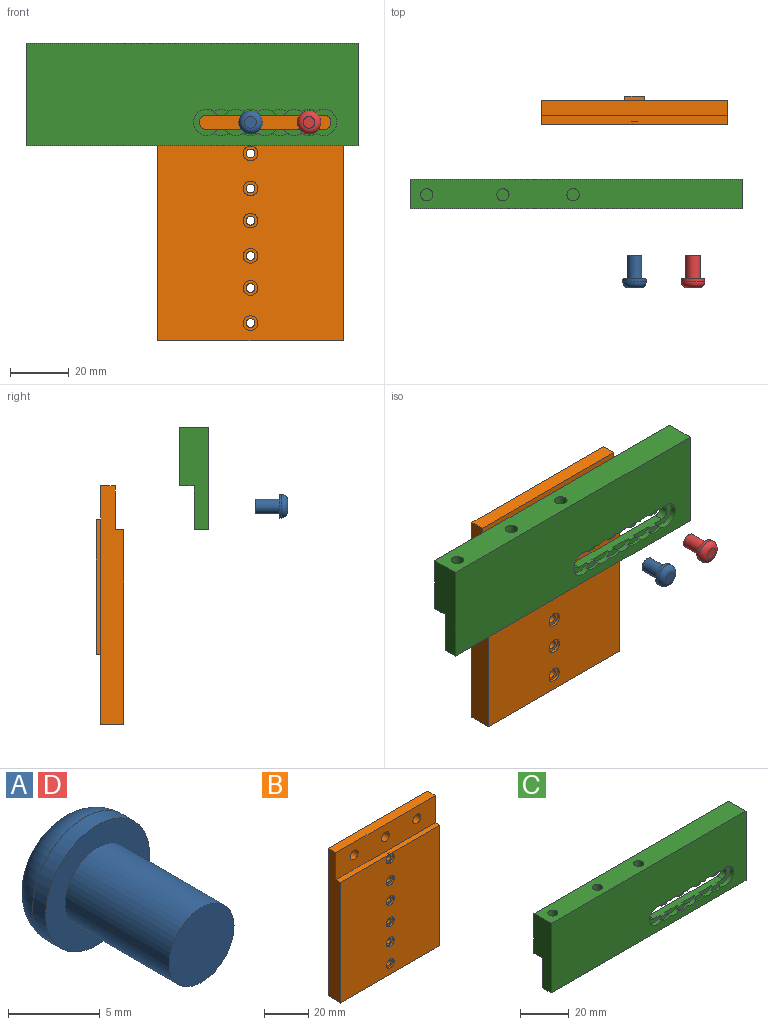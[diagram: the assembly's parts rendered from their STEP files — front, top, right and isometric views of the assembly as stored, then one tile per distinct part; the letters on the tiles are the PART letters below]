
ASSEMBLY  parts=4 mates=5
PART A: 6 faces, bbox 8.7x11x8.7 mm
  f0: cylinder r=2.5mm len=8mm, axis (0,1,0), area 125.7mm2, adj f1,f4
  f1: plane 5x5mm, normal (0,-1,0), area 19.6mm2, adj f0
  f2: cylinder r=4mm len=8mm, axis (0,-1,0), area 25.1mm2, adj f4,f5
  f3: plane 4x4mm, normal (0,1,0), area 12.6mm2, adj f5
  f4: plane 8x8mm, normal (0,-1,0), area 30.6mm2, adj f0,f2
  f5: torus R=2mm, axis (0,-1,0), area 64.6mm2, adj f2,f3
PART B: 34 faces, bbox 63.5x9.5x81.6 mm
  f0: plane 6.5x1.5mm, normal (0,0,1), area 9.7mm2, adj f1,f2,f14,f21
  f1: plane 46x1.5mm, normal (-1,0,0), area 69mm2, adj f0,f14,f16,f21
  f2: plane 46x1.5mm, normal (1,0,0), area 69mm2, adj f0,f14,f16,f21
  f3: plane 81.6x8mm, normal (1,0,0), area 607.8mm2, adj f4,f11,f13,f14,f15,f32
  f4: plane 63.5x3mm, normal (0,0,1), area 190.5mm2, adj f3,f5,f13,f15
  f5: plane 81.6x8mm, normal (-1,0,0), area 607.8mm2, adj f4,f11,f13,f14,f15,f32
  f6: cylinder r=2.5mm len=5mm, axis (0,1,0), area 15.7mm2, adj f13,f27
  f7: cylinder r=2.5mm len=5mm, axis (0,1,0), area 15.7mm2, adj f13,f28
  f8: cylinder r=2.5mm len=5mm, axis (0,1,0), area 15.7mm2, adj f13,f29
  f9: cylinder r=2.5mm len=5mm, axis (0,1,0), area 15.7mm2, adj f13,f23
  f10: cylinder r=2.5mm len=5mm, axis (0,1,0), area 15.7mm2, adj f13,f25
  f11: plane 63.5x8mm, normal (0,0,-1), area 508mm2, adj f3,f5,f13,f14
  f12: cylinder r=2.5mm len=5mm, axis (0,1,0), area 15.7mm2, adj f13,f26
  f13: plane 66.6x63.5mm, normal (0,-1,0), area 4111.3mm2, adj f3,f4,f5,f6,f7,f8,f9,f10
  f14: plane 81.6x63.5mm, normal (0,1,0), area 4809.6mm2, adj f0,f1,f2,f3,f5,f11,f16,f22
  f15: plane 63.5x15mm, normal (0,-1,0), area 893.6mm2, adj f3,f4,f5,f30,f31,f32,f33
  f16: plane 6.5x1.5mm, normal (0,0,-1), area 9.7mm2, adj f1,f2,f14,f21
  f17: cylinder r=1.5mm len=8.5mm, axis (0,-1,0), area 80.1mm2, adj f21,f28
  f18: cylinder r=1.5mm len=8.5mm, axis (0,-1,0), area 80.1mm2, adj f21,f27
  f19: cylinder r=1.5mm len=8.5mm, axis (0,-1,0), area 80.1mm2, adj f21,f26
  f20: cylinder r=1.5mm len=8.5mm, axis (0,-1,0), area 80.1mm2, adj f21,f29
  f21: plane 46x6.5mm, normal (0,1,0), area 270.7mm2, adj f0,f1,f2,f16,f17,f18,f19,f20
  f22: cylinder r=1.5mm len=7mm, axis (0,1,0), area 66mm2, adj f14,f23
  f23: plane 5x5mm, normal (0,-1,0), area 12.6mm2, adj f9,f22
  f24: cylinder r=1.5mm len=7mm, axis (0,1,0), area 66mm2, adj f14,f25
  f25: plane 5x5mm, normal (0,-1,0), area 12.6mm2, adj f10,f24
  f26: plane 5x5mm, normal (0,-1,0), area 12.6mm2, adj f12,f19
  f27: plane 5x5mm, normal (0,-1,0), area 12.6mm2, adj f6,f18
  f28: plane 5x5mm, normal (0,-1,0), area 12.6mm2, adj f7,f17
  f29: plane 5x5mm, normal (0,-1,0), area 12.6mm2, adj f8,f20
  f30: cylinder r=2.5mm len=5mm, axis (0,-1,0), area 78.5mm2, adj f14,f15
  f31: cylinder r=2.5mm len=5mm, axis (0,-1,0), area 78.5mm2, adj f14,f15
  f32: plane 63.5x5mm, normal (0,0,1), area 317.5mm2, adj f3,f5,f14,f15
  f33: cylinder r=2.5mm len=5mm, axis (0,-1,0), area 78.5mm2, adj f14,f15
PART C: 50 faces, bbox 113.5x10x35 mm
  f0: plane 113.5x10mm, normal (0,0,1), area 1093.4mm2, adj f1,f16,f18,f43,f44,f46,f48
  f1: plane 113.5x35mm, normal (0,-1,0), area 3568.4mm2, adj f0,f4,f5,f6,f7,f8,f9,f10
  f2: plane 40x4mm, normal (0,0,1), area 130.1mm2, adj f4,f8,f9,f10,f11,f12,f13,f14
  f3: plane 40x4mm, normal (0,0,-1), area 130.1mm2, adj f4,f5,f6,f7,f8,f12,f13,f14
  f4: cylinder r=4.5mm len=9mm, axis (0,1,0), area 42.4mm2, adj f1,f2,f3,f19,f33,f34,f41,f42
  f5: cylinder r=4.5mm len=7.48mm, axis (0,1,0), area 14.1mm2, adj f1,f3,f20,f39,f40,f41,f42
  f6: cylinder r=4.5mm len=7.48mm, axis (0,1,0), area 14.1mm2, adj f1,f3,f21,f37,f38,f39,f40
  f7: cylinder r=4.5mm len=7.48mm, axis (0,1,0), area 14.1mm2, adj f1,f3,f22,f35,f36,f37,f38
  f8: cylinder r=4.5mm len=9mm, axis (0,1,0), area 42.4mm2, adj f1,f2,f3,f23,f27,f28,f35,f36
  f9: cylinder r=4.5mm len=7.48mm, axis (0,1,0), area 14.1mm2, adj f1,f2,f24,f31,f32,f33,f34
  f10: cylinder r=4.5mm len=7.48mm, axis (0,1,0), area 14.1mm2, adj f1,f2,f25,f29,f30,f31,f32
  f11: cylinder r=4.5mm len=7.48mm, axis (0,1,0), area 14.1mm2, adj f1,f2,f26,f27,f28,f29,f30
  f12: cylinder r=2.5mm len=5mm, axis (0,1,0), area 23.6mm2, adj f2,f3,f14,f19
  f13: cylinder r=2.5mm len=5mm, axis (0,1,0), area 23.6mm2, adj f2,f3,f14,f23
  f14: plane 113.5x15mm, normal (0,1,0), area 1482.9mm2, adj f2,f3,f12,f13,f15,f16,f17,f43
  f15: plane 113.5x5mm, normal (0,0,-1), area 567.5mm2, adj f1,f14,f16,f43
  f16: plane 35x10mm, normal (1,0,0), area 275mm2, adj f0,f1,f14,f15,f17,f18
  f17: plane 113.5x5mm, normal (0,0,-1), area 567.5mm2, adj f14,f16,f18,f43
  f18: plane 113.5x20mm, normal (0,1,0), area 2270mm2, adj f0,f16,f17,f43
  f19: plane 9x8.24mm, normal (0,-1,0), area 32.5mm2, adj f2,f3,f4,f12
  f20: plane 7.48x2mm, normal (0,-1,0), area 10.5mm2, adj f3,f5
  f21: plane 7.48x2mm, normal (0,-1,0), area 10.5mm2, adj f3,f6
  f22: plane 7.48x2mm, normal (0,-1,0), area 10.5mm2, adj f3,f7
  f23: plane 9x8.24mm, normal (0,-1,0), area 32.5mm2, adj f2,f3,f8,f13
  f24: plane 7.48x2mm, normal (0,-1,0), area 10.5mm2, adj f2,f9
  f25: plane 7.48x2mm, normal (0,-1,0), area 10.5mm2, adj f2,f10
  f26: plane 7.48x2mm, normal (0,-1,0), area 10.5mm2, adj f2,f11
  f27: cylinder r=4.5mm len=5mm, axis (0,1,0), area 5.3mm2, adj f1,f8,f11,f28
  f28: plane 5x2mm, normal (0,-1,0), area 7mm2, adj f2,f8,f11,f27
  f29: cylinder r=4.5mm len=5mm, axis (0,1,0), area 5.3mm2, adj f1,f10,f11,f30
  f30: plane 5x2mm, normal (0,-1,0), area 7mm2, adj f2,f10,f11,f29
  f31: cylinder r=4.5mm len=5mm, axis (0,1,0), area 5.3mm2, adj f1,f9,f10,f32
  f32: plane 5x2mm, normal (0,-1,0), area 7mm2, adj f2,f9,f10,f31
  f33: cylinder r=4.5mm len=5mm, axis (0,1,0), area 5.3mm2, adj f1,f4,f9,f34
  f34: plane 5x2mm, normal (0,-1,0), area 7mm2, adj f2,f4,f9,f33
  f35: cylinder r=4.5mm len=5mm, axis (0,1,0), area 5.3mm2, adj f1,f7,f8,f36
  f36: plane 5x2mm, normal (0,-1,0), area 7mm2, adj f3,f7,f8,f35
  f37: cylinder r=4.5mm len=5mm, axis (0,1,0), area 5.3mm2, adj f1,f6,f7,f38
  f38: plane 5x2mm, normal (0,-1,0), area 7mm2, adj f3,f6,f7,f37
  f39: cylinder r=4.5mm len=5mm, axis (0,1,0), area 5.3mm2, adj f1,f5,f6,f40
  f40: plane 5x2mm, normal (0,-1,0), area 7mm2, adj f3,f5,f6,f39
  f41: cylinder r=4.5mm len=5mm, axis (0,1,0), area 5.3mm2, adj f1,f4,f5,f42
  f42: plane 5x2mm, normal (0,-1,0), area 7mm2, adj f3,f4,f5,f41
  f43: plane 35x10mm, normal (-1,0,0), area 275mm2, adj f0,f1,f14,f15,f17,f18
  f44: cylinder r=2.1mm len=15mm, axis (0,0,1), area 197.9mm2, adj f0,f45
  f45: plane 4.2x4.2mm, normal (0,0,1), area 13.9mm2, adj f44
  f46: cylinder r=2.1mm len=15mm, axis (0,0,1), area 197.9mm2, adj f0,f47
  f47: plane 4.2x4.2mm, normal (0,0,1), area 13.9mm2, adj f46
  f48: cylinder r=2.1mm len=15mm, axis (0,0,1), area 197.9mm2, adj f0,f49
  f49: plane 4.2x4.2mm, normal (0,0,1), area 13.9mm2, adj f48
PART D: same geometry as A
PLACE A rot(axis=(1,0,0),180deg) t=(113.94,-59.68,-39.87)mm
PLACE B t=(11.28,-3.68,6.72)mm fixed
PLACE C t=(16.28,-30.68,6.72)mm
PLACE D rot(axis=(1,0,0),180deg) t=(133.94,-59.68,-39.87)mm
MATE slider D.f0 <-> B.f31  axis (0,1,0) through (93.94,-51.68,-72.92)mm
MATE planar D.f0 <-> A.f0  axis (0,-1,0) through (93.94,-59.68,-72.92)mm
MATE planar C.f17 <-> B.f32  axis (0,0,-1) through (110.69,-25.68,-65.92)mm
MATE slider A.f0 <-> B.f30  axis (0,1,0) through (73.94,-51.68,-72.92)mm
MATE slider C.f27 <-> D.f0  axis (0,-1,0) through (93.94,-34.68,-72.92)mm
